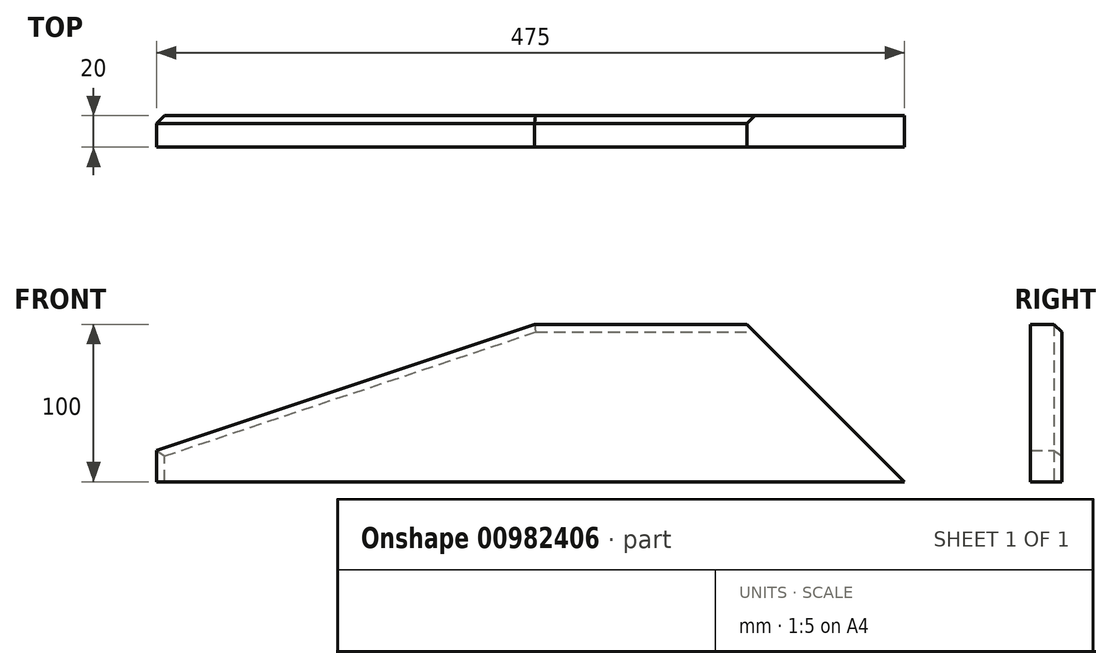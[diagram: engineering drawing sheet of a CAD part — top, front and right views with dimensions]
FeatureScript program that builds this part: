
annotation { "Feature Type Name" : "Feature", "Feature Type Description" : "" }
export const myFeature = defineFeature(function(context is Context, id is Id, definition is map)
    precondition{}
    {
        {
            var Q0;
            Q0=qCreatedBy(makeId("Front.planeOp"),FACE);
            var sketch = newSketch(context, id + "F0", { "sketchPlane" : qUnion([Q0])});
            skLineSegment(sketch, "E0.bottom", {"start": v(247.03, -18.12) * mm, "end": v(-227.97, -18.12) * mm});
            skLineSegment(sketch, "E0.top", {"start": v(247.03, 81.88) * mm, "end": v(12.03, 81.88) * mm});
            skLineSegment(sketch, "E0.left", {"start": v(247.03, -18.12) * mm, "end": v(247.03, 81.88) * mm});
            skLineSegment(sketch, "E0.right", {"start": v(-227.97, -18.12) * mm, "end": v(-227.97, 1.88) * mm});
            skPoint(sketch, "E0.middle", {"position": v(9.53, 31.88) * mm});
            skPoint(sketch, "E1", {"position": v(12.03, 81.88) * mm});
            skPoint(sketch, "E2", {"position": v(-227.97, 1.88) * mm});
            skLineSegment(sketch, "E3", {"start": v(-227.97, 1.88) * mm, "end": v(12.03, 81.88) * mm});
            skSolve(sketch);
        }
        {
            var Q0;
            Q0=qSketchRegion(id+"F0",true);
            extrude(context, id + "F1", {"entities" : qUnion([Q0]), "depth" : 20 * mm, "offsetDistance" : 25 * mm});
        }
        {
            var Q0;
            Q0=makeQuery(id+"F1.opExtrude","CAP_EDGE",EDGE,{"disambiguationData":[OSD([sQuery(id+"F0.wireOp",EDGE,"E0.top")])],"isStart":true});
            var Q1;
            Q1=makeQuery(id+"F1.opExtrude","CAP_EDGE",EDGE,{"disambiguationData":[OSD([sQuery(id+"F0.wireOp",EDGE,"E3")])],"isStart":true});
            var Q2;
            Q2=makeQuery(id+"F1.opExtrude","CAP_EDGE",EDGE,{"disambiguationData":[OSD([sQuery(id+"F0.wireOp",EDGE,"E0.right")])],"isStart":true});
            chamfer(context, id + "F2", {"entities" : qUnion([Q0, Q1, Q2]), "width" : 5 * mm, "tangentPropagation" : true});
        }
        {
            var Q0;
            Q0=makeQuery(id+"F1.opExtrude","SWEPT_EDGE",EDGE,{"disambiguationData":[OSD([sQuery(id+"F0.wireOp",EDGE,"E0.top"),sQuery(id+"F0.wireOp",EDGE,"E0.left")])]});
            chamfer(context, id + "F3", {"entities" : qUnion([Q0]), "width" : 100 * mm, "tangentPropagation" : true});
        }
    });
